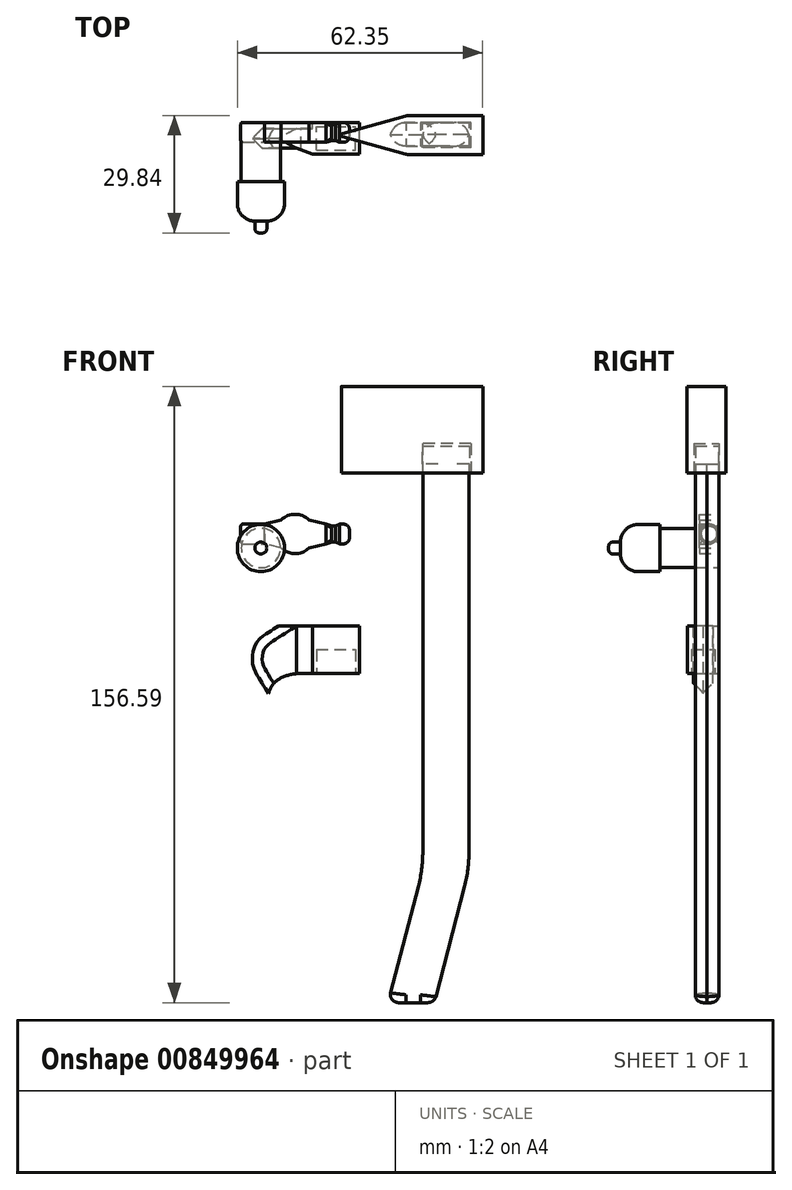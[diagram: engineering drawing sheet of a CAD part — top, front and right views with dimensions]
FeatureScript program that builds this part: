
annotation { "Feature Type Name" : "Feature", "Feature Type Description" : "" }
export const myFeature = defineFeature(function(context is Context, id is Id, definition is map)
    precondition{}
    {
        {
            var Q0;
            Q0=qCreatedBy(makeId("Front.planeOp"),FACE);
            var sketch = newSketch(context, id + "F0", { "sketchPlane" : qUnion([Q0])});
            skLineSegment(sketch, "E0.bottom", {"start": v(0.87, 7.59) * mm, "end": v(12.87, 7.59) * mm});
            skLineSegment(sketch, "E0.top", {"start": v(0.87, -4.41) * mm, "end": v(12.87, -4.41) * mm});
            skLineSegment(sketch, "E0.left", {"start": v(0.87, 7.59) * mm, "end": v(0.87, -4.41) * mm});
            skLineSegment(sketch, "E0.right", {"start": v(12.87, 7.59) * mm, "end": v(12.87, -4.41) * mm});
            skSolve(sketch);
        }
        {
            var Q0;
            Q0=makeQuery(id+"F0.imprint","IMPRINT",FACE,{"disambiguationData":[TD([[makeQuery(id+"F0.imprint","IMPRINT",EDGE,{"derivedFrom":sQuery(id+"F0.wireOp",EDGE,"E0.bottom")}),-1.0]])]});
            extrude(context, id + "F1", {"entities" : qUnion([Q0]), "depth" : 8 * mm, "offsetDistance" : 25.4 * mm});
        }
        {
            var Q0;
            Q0=makeQuery(id+"F1.opExtrude","CAP_FACE",FACE,{"disambiguationData":[OSD([sQuery(id+"F0.wireOp",EDGE,"E0.bottom"),sQuery(id+"F0.wireOp",EDGE,"E0.top"),sQuery(id+"F0.wireOp",EDGE,"E0.left"),sQuery(id+"F0.wireOp",EDGE,"E0.right")])],"isStart":false});
            cPlane(context, id + "F2", {"entities" : qUnion([Q0]), "cplaneType" : CPlaneType.OFFSET, "offset" : 4 * mm, "oppositeDirection" : true, "width" : 152.4 * mm, "height" : 152.4 * mm});
        }
        {
            var Q0;
            Q0=qCreatedBy(id+"F2.planeOp",FACE);
            var sketch = newSketch(context, id + "F3", { "sketchPlane" : qUnion([Q0])});
            skLineSegment(sketch, "E1.bottom", {"start": v(0.9, 7.6) * mm, "end": v(12.9, 7.6) * mm});
            skLineSegment(sketch, "E1.top", {"start": v(0.9, -4.4) * mm, "end": v(12.9, -4.4) * mm});
            skLineSegment(sketch, "E1.left", {"start": v(0.9, 7.6) * mm, "end": v(0.9, -4.4) * mm});
            skLineSegment(sketch, "E1.right", {"start": v(12.9, 7.6) * mm, "end": v(12.9, -4.4) * mm});
            skLineSegment(sketch, "E2", {"start": v(0.9, 7.6) * mm, "end": v(-11.1, 7.6) * mm});
            skLineSegment(sketch, "E3", {"start": v(0.9, -4.4) * mm, "end": v(-2.06, -4.4) * mm});
            skFitSpline(sketch, "E4", {"points": [v(-11.1, 7.6) * mm, v(-15.07, 3.94) * mm, v(-16.04, -2.39) * mm, v(-14.17, -6.73) * mm, v(-10.18, -12.68) * mm], "startDerivative": vector(-19.1, -12.34) * mm, "endDerivative": vector(24.35, -33.73) * mm});
            skFitSpline(sketch, "E5", {"points": [v(-10.18, -12.68) * mm, v(-10.12, -9.14) * mm, v(-8.49, -6.53) * mm, v(-5.5, -4.96) * mm, v(-2.06, -4.4) * mm], "startDerivative": vector(-5.15, 10.72) * mm, "endDerivative": vector(13.38, 1) * mm});
            skSolve(sketch);
        }
        {
            var Q0;
            Q0=makeQuery(id+"F3.imprint","IMPRINT",FACE,{"disambiguationData":[TD([[makeQuery(id+"F3.imprint","IMPRINT",EDGE,{"derivedFrom":sQuery(id+"F3.wireOp",EDGE,"E1.left")}),-1.0]])]});
            extrude(context, id + "F4", {"entities" : qUnion([Q0]), "operationType" : NewBodyOperationType.ADD, "endBound" : BoundingType.SYMMETRIC, "depth" : 5 * mm, "offsetDistance" : 25.4 * mm});
        }
        {
            var Q0;
            Q0=makeQuery(id+"F4.opExtrude","CAP_EDGE",EDGE,{"disambiguationData":[OSD([sQuery(id+"F3.wireOp",EDGE,"E4")])],"isStart":false});
            var Q1;
            Q1=makeQuery(id+"F4.opExtrude","CAP_EDGE",EDGE,{"disambiguationData":[OSD([sQuery(id+"F3.wireOp",EDGE,"E4")])],"isStart":true});
            chamfer(context, id + "F5", {"entities" : qUnion([Q0, Q1]), "width" : 4.3 * mm, "tangentPropagation" : true});
        }
        {
            var Q0;
            Q0=makeQuery(id+"F1.opExtrude","SWEPT_FACE",FACE,{"disambiguationData":[OSD([sQuery(id+"F0.wireOp",EDGE,"E0.bottom")])]});
            var sketch = newSketch(context, id + "F6", { "sketchPlane" : qUnion([Q0])});
            skLineSegment(sketch, "E6", {"start": v(0.87, -8) * mm, "end": v(-3.15, -6.5) * mm});
            skLineSegment(sketch, "E7", {"start": v(-3.15, -6.5) * mm, "end": v(0.87, -6.5) * mm});
            skLineSegment(sketch, "E8", {"start": v(0.87, -6.5) * mm, "end": v(0.87, -8) * mm});
            skLineSegment(sketch, "E9", {"start": v(0.87, -1.5) * mm, "end": v(0.87, 0) * mm});
            skLineSegment(sketch, "E10", {"start": v(0.87, 0) * mm, "end": v(-3.2, -1.5) * mm});
            skLineSegment(sketch, "E11", {"start": v(-3.2, -1.5) * mm, "end": v(0.87, -1.5) * mm});
            skSolve(sketch);
        }
        {
            var Q0;
            Q0=makeQuery(id+"F6.imprint","IMPRINT",FACE,{"disambiguationData":[TD([[makeQuery(id+"F6.imprint","IMPRINT",EDGE,{"derivedFrom":sQuery(id+"F6.wireOp",EDGE,"E9")}),-1.0]])]});
            var Q1;
            Q1=makeQuery(id+"F6.imprint","IMPRINT",FACE,{"disambiguationData":[TD([[makeQuery(id+"F6.imprint","IMPRINT",EDGE,{"derivedFrom":sQuery(id+"F6.wireOp",EDGE,"E6")}),-1.0]])]});
            extrude(context, id + "F7", {"entities" : qUnion([Q0, Q1]), "operationType" : NewBodyOperationType.ADD, "oppositeDirection" : true, "depth" : 12 * mm, "offsetDistance" : 25.4 * mm});
        }
        {
            var Q0;
            Q0=makeQuery(id+"F7.boolean.opBoolean","MERGE",FACE,{"derivedFrom":[makeQuery(id+"F1.opExtrude","SWEPT_FACE",FACE,{"disambiguationData":[OSD([sQuery(id+"F0.wireOp",EDGE,"E0.top")])]}),makeQuery(id+"F7.opExtrude","CAP_FACE",FACE,{"disambiguationData":[OSD([sQuery(id+"F6.wireOp",EDGE,"E6"),sQuery(id+"F6.wireOp",EDGE,"E7"),sQuery(id+"F6.wireOp",EDGE,"E8")])],"isStart":false}),makeQuery(id+"F7.opExtrude","CAP_FACE",FACE,{"disambiguationData":[OSD([sQuery(id+"F6.wireOp",EDGE,"E9"),sQuery(id+"F6.wireOp",EDGE,"E10"),sQuery(id+"F6.wireOp",EDGE,"E11")])],"isStart":false})]});
            var sketch = newSketch(context, id + "F8", { "sketchPlane" : qUnion([Q0])});
            skPoint(sketch, "E12", {"position": v(6.87, 8) * mm});
            skPoint(sketch, "E13", {"position": v(12.87, 4) * mm});
            skPoint(sketch, "E14", {"position": v(6.87, 4) * mm});
            skLineSegment(sketch, "E15.bottom", {"start": v(1.87, 7) * mm, "end": v(11.87, 7) * mm});
            skLineSegment(sketch, "E15.top", {"start": v(1.87, 1) * mm, "end": v(11.87, 1) * mm});
            skLineSegment(sketch, "E15.left", {"start": v(1.87, 7) * mm, "end": v(1.87, 1) * mm});
            skLineSegment(sketch, "E15.right", {"start": v(11.87, 7) * mm, "end": v(11.87, 1) * mm});
            skSolve(sketch);
        }
        {
            var Q0;
            Q0=qCreatedBy(makeId("Front.planeOp"),FACE);
            var sketch = newSketch(context, id + "F9", { "sketchPlane" : qUnion([Q0])});
            skLineSegment(sketch, "E16", {"start": v(28.79, 48.76) * mm, "end": v(28.79, -54.24) * mm});
            skLineSegment(sketch, "E17", {"start": v(28.79, -54.24) * mm, "end": v(40.79, -54.24) * mm});
            skLineSegment(sketch, "E18", {"start": v(40.79, -54.24) * mm, "end": v(40.79, 48.76) * mm});
            skLineSegment(sketch, "E19", {"start": v(40.79, 48.76) * mm, "end": v(28.79, 48.76) * mm});
            skLineSegment(sketch, "E20", {"start": v(40.79, -54.24) * mm, "end": v(31.95, -88.1) * mm});
            skLineSegment(sketch, "E21", {"start": v(28.79, -54.24) * mm, "end": v(19.95, -88.1) * mm});
            skLineSegment(sketch, "E22", {"start": v(19.95, -88.1) * mm, "end": v(31.95, -88.1) * mm});
            skLineSegment(sketch, "E23", {"start": v(28.79, 48.76) * mm, "end": v(28.79, 53.26) * mm});
            skLineSegment(sketch, "E24", {"start": v(28.79, 53.26) * mm, "end": v(40.79, 53.26) * mm});
            skLineSegment(sketch, "E25", {"start": v(40.79, 53.26) * mm, "end": v(40.79, 48.76) * mm});
            skSolve(sketch);
        }
        {
            var Q0;
            Q0=makeQuery(id+"F9.imprint","IMPRINT",FACE,{"disambiguationData":[TD([[makeQuery(id+"F9.imprint","IMPRINT",EDGE,{"derivedFrom":sQuery(id+"F9.wireOp",EDGE,"E16")}),1.0]])]});
            var Q1;
            Q1=makeQuery(id+"F9.imprint","IMPRINT",FACE,{"disambiguationData":[TD([[makeQuery(id+"F9.imprint","IMPRINT",EDGE,{"derivedFrom":sQuery(id+"F9.wireOp",EDGE,"E17")}),-1.0]])]});
            extrude(context, id + "F10", {"entities" : qUnion([Q0, Q1]), "depth" : 6 * mm, "offsetDistance" : 25.4 * mm});
        }
        {
            var Q0;
            Q0=makeQuery(id+"F10.opExtrude","SWEPT_EDGE",EDGE,{"disambiguationData":[OSD([sQuery(id+"F9.wireOp",EDGE,"E17"),sQuery(id+"F9.wireOp",EDGE,"E18"),sQuery(id+"F9.wireOp",EDGE,"E20")])]});
            var Q1;
            Q1=makeQuery(id+"F10.opExtrude","SWEPT_EDGE",EDGE,{"disambiguationData":[OSD([sQuery(id+"F9.wireOp",EDGE,"E16"),sQuery(id+"F9.wireOp",EDGE,"E17"),sQuery(id+"F9.wireOp",EDGE,"E21")])]});
            fillet(context, id + "F11", {"entities" : qUnion([Q0, Q1]), "radius" : 35 * mm, "tangentPropagation" : true, "allowEdgeOverflow" : false});
        }
        {
            var Q0;
            Q0=makeQuery(id+"F10.opExtrude","CAP_EDGE",EDGE,{"disambiguationData":[OSD([sQuery(id+"F9.wireOp",EDGE,"E18")])],"isStart":false});
            var Q1;
            Q1=makeQuery(id+"F10.opExtrude","CAP_EDGE",EDGE,{"disambiguationData":[OSD([sQuery(id+"F9.wireOp",EDGE,"E18")])],"isStart":true});
            var Q2;
            Q2=makeQuery(id+"F10.opExtrude","CAP_EDGE",EDGE,{"disambiguationData":[OSD([sQuery(id+"F9.wireOp",EDGE,"E16")])],"isStart":false});
            var Q3;
            Q3=makeQuery(id+"F10.opExtrude","CAP_EDGE",EDGE,{"disambiguationData":[OSD([sQuery(id+"F9.wireOp",EDGE,"E16")])],"isStart":true});
            fillet(context, id + "F12", {"entities" : qUnion([Q0, Q1, Q2, Q3]), "radius" : 4 * mm, "tangentPropagation" : true, "allowEdgeOverflow" : false});
        }
        {
            var Q0;
            Q0=makeQuery(id+"F9.imprint","IMPRINT",FACE,{"disambiguationData":[TD([[makeQuery(id+"F9.imprint","IMPRINT",EDGE,{"derivedFrom":sQuery(id+"F9.wireOp",EDGE,"E19")}),-1.0]])]});
            extrude(context, id + "F13", {"entities" : qUnion([Q0]), "operationType" : NewBodyOperationType.ADD, "depth" : 6 * mm, "offsetDistance" : 25.4 * mm});
        }
        {
            var Q0;
            Q0=makeQuery(id+"F8.imprint","IMPRINT",FACE,{"disambiguationData":[TD([[makeQuery(id+"F8.imprint","IMPRINT",EDGE,{"derivedFrom":sQuery(id+"F8.wireOp",EDGE,"E15.bottom")}),-1.0]])]});
            extrude(context, id + "F14", {"entities" : qUnion([Q0]), "operationType" : NewBodyOperationType.REMOVE, "oppositeDirection" : true, "depth" : 6 * mm, "offsetDistance" : 25.4 * mm});
        }
        {
            var Q0;
            Q0=qCreatedBy(makeId("Top.planeOp"),FACE);
            var sketch = newSketch(context, id + "F15", { "sketchPlane" : qUnion([Q0])});
            skLineSegment(sketch, "E26.bottom", {"start": v(-10.92, 14.8) * mm, "end": v(8.08, 14.8) * mm});
            skLineSegment(sketch, "E26.top", {"start": v(-10.92, 4.8) * mm, "end": v(8.08, 4.8) * mm});
            skLineSegment(sketch, "E26.left", {"start": v(-10.92, 14.8) * mm, "end": v(-10.92, 4.8) * mm});
            skLineSegment(sketch, "E26.right", {"start": v(8.08, 14.8) * mm, "end": v(8.08, 4.8) * mm});
            skPoint(sketch, "E27", {"position": v(-10.92, 9.8) * mm});
            skPoint(sketch, "E28", {"position": v(-28.92, 9.8) * mm});
            skLineSegment(sketch, "E29", {"start": v(-28.92, 9.8) * mm, "end": v(-10.92, 14.8) * mm});
            skLineSegment(sketch, "E30", {"start": v(-28.92, 9.8) * mm, "end": v(-10.92, 4.8) * mm});
            skPoint(sketch, "E31", {"position": v(8.08, 9.8) * mm});
            skSolve(sketch);
        }
        {
            var Q0;
            Q0=makeQuery(id+"F15.imprint","IMPRINT",FACE,{"disambiguationData":[TD([[makeQuery(id+"F15.imprint","IMPRINT",EDGE,{"derivedFrom":sQuery(id+"F15.wireOp",EDGE,"E26.bottom")}),-1.0]])]});
            var Q1;
            Q1=makeQuery(id+"F15.imprint","IMPRINT",FACE,{"disambiguationData":[TD([[makeQuery(id+"F15.imprint","IMPRINT",EDGE,{"derivedFrom":sQuery(id+"F15.wireOp",EDGE,"E26.left")}),-1.0]])]});
            extrude(context, id + "F16", {"entities" : qUnion([Q0, Q1]), "depth" : 22 * mm, "offsetDistance" : 25.4 * mm});
        }
        {
            var Q0;
            Q0=makeQuery(id+"F16.opExtrude","SWEPT_EDGE",EDGE,{"disambiguationData":[OSD([sQuery(id+"F15.wireOp",EDGE,"E29"),sQuery(id+"F15.wireOp",EDGE,"E30")])]});
            fillet(context, id + "F17", {"entities" : qUnion([Q0]), "radius" : .4 * mm, "tangentPropagation" : true, "allowEdgeOverflow" : false});
        }
        {
            var Q0;
            Q0=makeQuery(id+"F16.opExtrude","SWEPT_EDGE",EDGE,{"disambiguationData":[OSD([sQuery(id+"F15.wireOp",EDGE,"E26.top"),sQuery(id+"F15.wireOp",EDGE,"E26.left"),sQuery(id+"F15.wireOp",EDGE,"E30")])]});
            var Q1;
            Q1=makeQuery(id+"F16.opExtrude","SWEPT_EDGE",EDGE,{"disambiguationData":[OSD([sQuery(id+"F15.wireOp",EDGE,"E26.bottom"),sQuery(id+"F15.wireOp",EDGE,"E26.left"),sQuery(id+"F15.wireOp",EDGE,"E29")])]});
            fillet(context, id + "F18", {"entities" : qUnion([Q0, Q1]), "radius" : 5.08 * mm, "tangentPropagation" : true, "allowEdgeOverflow" : false});
        }
        {
            var Q0;
            Q0=makeQuery(id+"F16.opExtrude","CAP_FACE",FACE,{"disambiguationData":[OSD([sQuery(id+"F15.wireOp",EDGE,"E26.bottom"),sQuery(id+"F15.wireOp",EDGE,"E26.top"),sQuery(id+"F15.wireOp",EDGE,"E26.right"),sQuery(id+"F15.wireOp",EDGE,"E29"),sQuery(id+"F15.wireOp",EDGE,"E30")])],"isStart":true});
            var sketch = newSketch(context, id + "F19", { "sketchPlane" : qUnion([Q0])});
            skPoint(sketch, "E32", {"position": v(8.08, -9.8) * mm});
            skPoint(sketch, "E33", {"position": v(-1.08, -4.8) * mm});
            skPoint(sketch, "E34", {"position": v(-1.08, -9.8) * mm});
            skLineSegment(sketch, "E35.bottom", {"start": v(5.12, -6.6) * mm, "end": v(-7.28, -6.6) * mm});
            skLineSegment(sketch, "E35.top", {"start": v(5.12, -13) * mm, "end": v(-7.28, -13) * mm});
            skLineSegment(sketch, "E35.left", {"start": v(5.12, -6.6) * mm, "end": v(5.12, -13) * mm});
            skLineSegment(sketch, "E35.right", {"start": v(-7.28, -6.6) * mm, "end": v(-7.28, -13) * mm});
            skSolve(sketch);
        }
        {
            var Q0;
            Q0=makeQuery(id+"F19.imprint","IMPRINT",FACE,{"disambiguationData":[TD([[makeQuery(id+"F19.imprint","IMPRINT",EDGE,{"derivedFrom":sQuery(id+"F19.wireOp",EDGE,"E35.bottom")}),1.0]])]});
            extrude(context, id + "F20", {"entities" : qUnion([Q0]), "operationType" : NewBodyOperationType.REMOVE, "oppositeDirection" : true, "depth" : 7.5 * mm, "offsetDistance" : 25.4 * mm});
        }
        {
            var Q0;
            Q0=makeQuery(id+"F10.opExtrude","SWEPT_FACE",FACE,{"disambiguationData":[OSD([sQuery(id+"F9.wireOp",EDGE,"E22")])]});
            fillet(context, id + "F21", {"entities" : qUnion([Q0]), "radius" : 2 * mm, "tangentPropagation" : true, "allowEdgeOverflow" : false});
        }
        {
            var Q0;
            Q0=makeQuery(id+"F16.opExtrude","SWEPT_BODY",BODY,{"disambiguationData":[OSD([sQuery(id+"F15.wireOp",EDGE,"E26.bottom"),sQuery(id+"F15.wireOp",EDGE,"E26.top"),sQuery(id+"F15.wireOp",EDGE,"E26.right"),sQuery(id+"F15.wireOp",EDGE,"E29"),sQuery(id+"F15.wireOp",EDGE,"E30")])]});
            transform(context, id + "F22", {"entities" : qUnion([Q0]), "transformType" : TransformType.TRANSLATION_3D, "dx" : 36.07 * mm, "dy" : -12.95 * mm, "dz" : 46.48 * mm, "makeCopy" : false});
        }
        {
            var Q0;
            Q0=qCreatedBy(makeId("Front.planeOp"),FACE);
            var sketch = newSketch(context, id + "F23", { "sketchPlane" : qUnion([Q0])});
            skArc(sketch, "E36", {"start": v(-7.04, 27.41) * mm, "mid": v(-3.53, 25.97) * mm, "end": v(-0.01, 27.41) * mm});
            skLineSegment(sketch, "E37", {"start": v(-7.04, 34.52) * mm, "end": v(-11.33, 33.5) * mm});
            skLineSegment(sketch, "E38.MirrorCS", {"start": v(-7.04, 27.41) * mm, "end": v(-11.33, 28.44) * mm});
            skLineSegment(sketch, "E39.MirrorCS", {"start": v(-0.01, 34.52) * mm, "end": v(4.28, 33.5) * mm});
            skLineSegment(sketch, "E40.MirrorCS", {"start": v(-0.01, 27.41) * mm, "end": v(4.28, 28.44) * mm});
            skLineSegment(sketch, "E41", {"start": v(-11.33, 28.44) * mm, "end": v(-11.33, 33.5) * mm});
            skLineSegment(sketch, "E42", {"start": v(4.28, 33.5) * mm, "end": v(4.28, 28.44) * mm});
            skArc(sketch, "E43.trimOffspring", {"start": v(-0.01, 34.52) * mm, "mid": v(-3.53, 35.97) * mm, "end": v(-7.04, 34.52) * mm});
            skSolve(sketch);
        }
        {
            var Q0;
            Q0=makeQuery(id+"F23.imprint","IMPRINT",FACE,{"disambiguationData":[TD([[makeQuery(id+"F23.imprint","IMPRINT",EDGE,{"derivedFrom":sQuery(id+"F23.wireOp",EDGE,"E36")}),1.0]])]});
            extrude(context, id + "F24", {"entities" : qUnion([Q0]), "depth" : 5 * mm, "offsetDistance" : 25.4 * mm});
        }
        {
            var Q0;
            Q0=makeQuery(id+"F24.opExtrude","SWEPT_FACE",FACE,{"disambiguationData":[OSD([sQuery(id+"F23.wireOp",EDGE,"E41")])]});
            var sketch = newSketch(context, id + "F25", { "sketchPlane" : qUnion([Q0])});
            skPoint(sketch, "E44", {"position": v(2.5, 33.5) * mm});
            skPoint(sketch, "E45", {"position": v(0, 30.97) * mm});
            skPoint(sketch, "E46", {"position": v(2.5, 30.97) * mm});
            skCircle(sketch, "E47", {"center": v(2.5, 30.97) * mm, "radius": 2.5 * mm});
            skSolve(sketch);
        }
        {
            var Q0;
            {var subQ0=sQuery(id+"F25.wireOp",EDGE,"E47");var subQ1=sQuery(id+"F23.wireOp",EDGE,"E41");var subQ2=makeQuery(id+"F25.imprint","INTERSECT",VERTEX,{"derivedFrom":[makeQuery(id+"F24.opExtrude","CAP_EDGE",EDGE,{"disambiguationData":[OSD([subQ1])],"isStart":true}),subQ0]});Q0=makeQuery(id+"F25.imprint","IMPRINT",FACE,{"disambiguationData":[TD([[makeQuery(id+"F25.imprint","IMPRINT",EDGE,{"disambiguationData":[TD([[subQ2,1.0]])],"derivedFrom":subQ0}),1.0]])]});}
            extrude(context, id + "F26", {"entities" : qUnion([Q0]), "operationType" : NewBodyOperationType.ADD, "depth" : 6 * mm, "offsetDistance" : 25.4 * mm});
        }
        {
            var Q0;
            Q0=makeQuery(id+"F26.opExtrude","CAP_FACE",FACE,{"disambiguationData":[OSD([sQuery(id+"F25.wireOp",EDGE,"E47")])],"isStart":false});
            fillet(context, id + "F27", {"entities" : qUnion([Q0]), "radius" : .5 * mm, "tangentPropagation" : true, "allowEdgeOverflow" : false});
        }
        {
            var Q0;
            Q0=makeQuery(id+"F24.opExtrude","SWEPT_FACE",FACE,{"disambiguationData":[OSD([sQuery(id+"F23.wireOp",EDGE,"E42")])]});
            cPlane(context, id + "F28", {"entities" : qUnion([Q0]), "cplaneType" : CPlaneType.OFFSET, "offset" : 1.5 * mm, "width" : 152.4 * mm, "height" : 152.4 * mm});
        }
        {
            var Q0;
            Q0=qCreatedBy(id+"F28.planeOp",FACE);
            var sketch = newSketch(context, id + "F29", { "sketchPlane" : qUnion([Q0])});
            skLineSegment(sketch, "E48.bottom", {"start": v(-5, 33.5) * mm, "end": v(0, 33.5) * mm});
            skLineSegment(sketch, "E48.top", {"start": v(-5, 28.44) * mm, "end": v(0, 28.44) * mm});
            skLineSegment(sketch, "E48.left", {"start": v(-5, 33.5) * mm, "end": v(-5, 28.44) * mm});
            skLineSegment(sketch, "E48.right", {"start": v(0, 33.5) * mm, "end": v(0, 28.44) * mm});
            skPoint(sketch, "E49", {"position": v(-2.5, 33.5) * mm});
            skPoint(sketch, "E50", {"position": v(-5, 30.97) * mm});
            skPoint(sketch, "E51", {"position": v(-2.5, 30.97) * mm});
            skCircle(sketch, "E52", {"center": v(-2.5, 30.97) * mm, "radius": 2.04 * mm});
            skSolve(sketch);
        }
        {
            var Q0;
            Q0=makeQuery(id+"F29.imprint","IMPRINT",FACE,{"disambiguationData":[TD([[makeQuery(id+"F29.imprint","IMPRINT",EDGE,{"derivedFrom":sQuery(id+"F29.wireOp",EDGE,"E52")}),1.0]])]});
            extrude(context, id + "F30", {"entities" : qUnion([Q0]), "depth" : 1 * mm, "offsetDistance" : 25.4 * mm});
        }
        {
            var Q1;
            Q1=makeQuery(id+"F30.opExtrude","CAP_FACE",FACE,{"disambiguationData":[OSD([sQuery(id+"F29.wireOp",EDGE,"E52")])],"isStart":true});
            var Q2;
            Q2=makeQuery(id+"F24.opExtrude","SWEPT_FACE",FACE,{"disambiguationData":[OSD([sQuery(id+"F23.wireOp",EDGE,"E42")])]});
            loft(context, id + "F31", {"operationType" : NewBodyOperationType.ADD, "sheetProfilesArray" : [{ "sheetProfileEntities" : qUnion([Q1]) }, { "sheetProfileEntities" : qUnion([Q2]) }]});
        }
        {
            var Q0;
            Q0=makeQuery(id+"F30.opExtrude","CAP_FACE",FACE,{"disambiguationData":[OSD([sQuery(id+"F29.wireOp",EDGE,"E52")])],"isStart":false});
            cPlane(context, id + "F32", {"entities" : qUnion([Q0]), "cplaneType" : CPlaneType.OFFSET, "offset" : 1 * mm, "width" : 152.4 * mm, "height" : 152.4 * mm});
        }
        {
            var Q0;
            Q0=qCreatedBy(id+"F32.planeOp",FACE);
            var sketch = newSketch(context, id + "F33", { "sketchPlane" : qUnion([Q0])});
            skCircle(sketch, "E53", {"center": v(-2.5, 30.97) * mm, "radius": 2.5 * mm});
            skSolve(sketch);
        }
        {
            var Q0;
            Q0=makeQuery(id+"F33.imprint","IMPRINT",FACE,{"disambiguationData":[TD([[makeQuery(id+"F33.imprint","IMPRINT",EDGE,{"derivedFrom":sQuery(id+"F33.wireOp",EDGE,"E53")}),1.0]])]});
            extrude(context, id + "F34", {"entities" : qUnion([Q0]), "depth" : 2.5 * mm, "offsetDistance" : 25.4 * mm});
        }
        {
            var Q0;
            Q0=makeQuery(id+"F34.opExtrude","CAP_FACE",FACE,{"disambiguationData":[OSD([sQuery(id+"F33.wireOp",EDGE,"E53")])],"isStart":true});
            var Q1;
            Q1=makeQuery(id+"F30.opExtrude","CAP_FACE",FACE,{"disambiguationData":[OSD([sQuery(id+"F29.wireOp",EDGE,"E52")])],"isStart":false});
            loft(context, id + "F35", {"operationType" : NewBodyOperationType.ADD, "sheetProfilesArray" : [{ "sheetProfileEntities" : qUnion([Q0]) }, { "sheetProfileEntities" : qUnion([Q1]) }]});
        }
        {
            var Q0;
            Q0=makeQuery(id+"F34.opExtrude","CAP_FACE",FACE,{"disambiguationData":[OSD([sQuery(id+"F33.wireOp",EDGE,"E53")])],"isStart":false});
            fillet(context, id + "F36", {"entities" : qUnion([Q0]), "radius" : 1.5 * mm, "tangentPropagation" : true, "allowEdgeOverflow" : false});
        }
        {
            var Q0;
            Q0=qCreatedBy(makeId("Front.planeOp"),FACE);
            var sketch = newSketch(context, id + "F37", { "sketchPlane" : qUnion([Q0])});
            skCircle(sketch, "E54", {"center": v(-12.21, 27.4) * mm, "radius": 5 * mm});
            skSolve(sketch);
        }
        {
            var Q0;
            Q0=makeQuery(id+"F37.imprint","IMPRINT",FACE,{"disambiguationData":[TD([[makeQuery(id+"F37.imprint","IMPRINT",EDGE,{"derivedFrom":sQuery(id+"F37.wireOp",EDGE,"E54")}),1.0]])]});
            extrude(context, id + "F38", {"entities" : qUnion([Q0]), "depth" : 17 * mm, "offsetDistance" : 25.4 * mm});
        }
        {
            var Q0;
            Q0=makeQuery(id+"F38.opExtrude","CAP_FACE",FACE,{"disambiguationData":[OSD([sQuery(id+"F37.wireOp",EDGE,"E54")])],"isStart":false});
            var sketch = newSketch(context, id + "F39", { "sketchPlane" : qUnion([Q0])});
            skCircle(sketch, "E55", {"center": v(-12.21, 27.4) * mm, "radius": 6 * mm});
            skSolve(sketch);
        }
        {
            var Q0;
            Q0=makeQuery(id+"F39.imprint","IMPRINT",FACE,{"disambiguationData":[TD([[makeQuery(id+"F39.imprint","IMPRINT",EDGE,{"derivedFrom":makeQuery(id+"F38.opExtrude","CAP_EDGE",EDGE,{"disambiguationData":[OSD([sQuery(id+"F37.wireOp",EDGE,"E54")])],"isStart":false})}),1.0]])]});
            var Q1;
            Q1=makeQuery(id+"F39.imprint","IMPRINT",FACE,{"disambiguationData":[TD([[makeQuery(id+"F39.imprint","IMPRINT",EDGE,{"derivedFrom":sQuery(id+"F39.wireOp",EDGE,"E55")}),1.0]])]});
            extrude(context, id + "F40", {"entities" : qUnion([Q0, Q1]), "depth" : 8 * mm, "offsetDistance" : 25.4 * mm});
        }
        {
            var Q0;
            Q0=makeQuery(id+"F40.opExtrude","CAP_FACE",FACE,{"disambiguationData":[OSD([sQuery(id+"F39.wireOp",EDGE,"E55")])],"isStart":false});
            fillet(context, id + "F41", {"entities" : qUnion([Q0]), "tangentPropagation" : true, "radius" : 4.5 * mm, "defaultsChanged" : true, "vertexSettings" : [], "allowEdgeOverflow" : false});
        }
        {
            var Q0;
            Q0=makeQuery(id+"F40.opExtrude","CAP_FACE",FACE,{"disambiguationData":[OSD([sQuery(id+"F39.wireOp",EDGE,"E55")])],"isStart":false});
            extrude(context, id + "F42", {"entities" : qUnion([Q0]), "operationType" : NewBodyOperationType.ADD, "depth" : 3 * mm, "offsetDistance" : 25.4 * mm});
        }
        {
            var Q0;
            Q0=makeQuery(id+"F42.opExtrude","CAP_FACE",FACE,{"disambiguationData":[OSD([sQuery(id+"F39.wireOp",EDGE,"E55")])],"isStart":false});
            fillet(context, id + "F43", {"entities" : qUnion([Q0]), "tangentPropagation" : true, "radius" : 1 * mm, "defaultsChanged" : true, "vertexSettings" : [], "allowEdgeOverflow" : false});
        }
        {
            var Q0;
            Q0=makeQuery(id+"F40.opExtrude","CAP_FACE",FACE,{"disambiguationData":[OSD([sQuery(id+"F39.wireOp",EDGE,"E55")])],"isStart":true});
            extrude(context, id + "F44", {"entities" : qUnion([Q0]), "operationType" : NewBodyOperationType.ADD, "depth" : 2 * mm, "offsetDistance" : 25.4 * mm});
        }
    });
